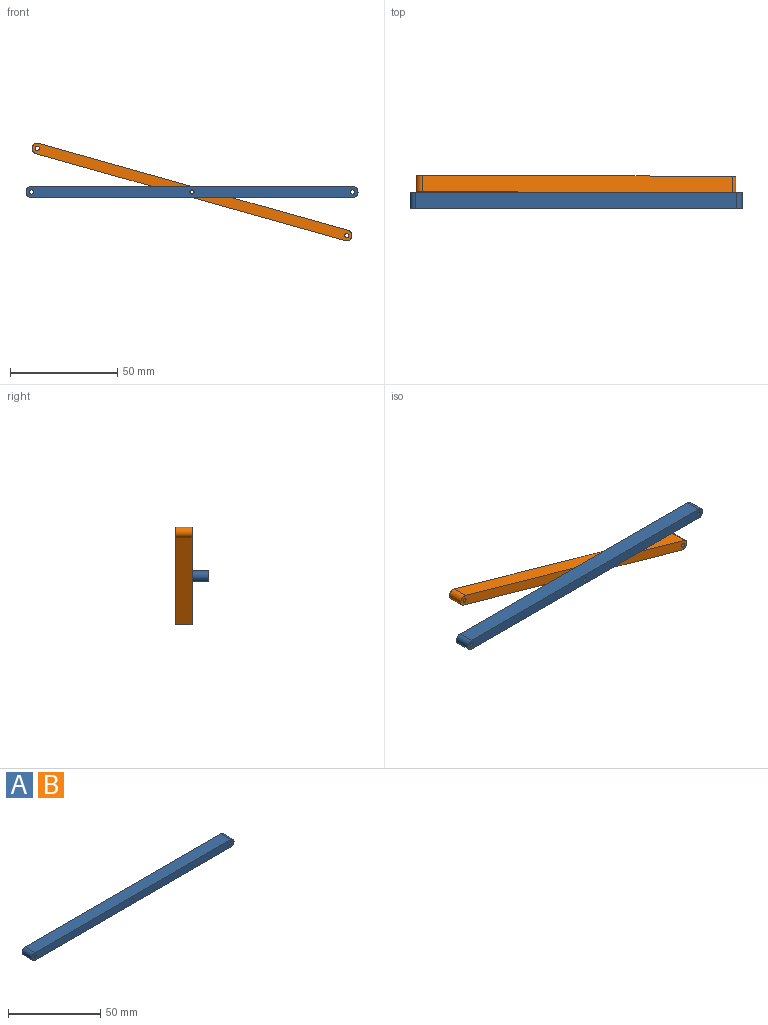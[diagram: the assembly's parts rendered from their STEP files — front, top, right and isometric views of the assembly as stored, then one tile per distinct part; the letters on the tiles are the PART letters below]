
ASSEMBLY  parts=2 mates=1
PART A: 9 faces, bbox 155x7.5x5 mm
  f0: plane 150x7.5mm, normal (0,0,1), area 1125mm2, adj f1,f6,f7,f8
  f1: cylinder r=2.5mm len=7.5mm, axis (0,1,0), area 58.9mm2, adj f0,f2,f7,f8
  f2: plane 150x7.5mm, normal (0,0,-1), area 1125mm2, adj f1,f6,f7,f8
  f3: cylinder r=1mm len=7.5mm, axis (0,1,0), area 47.1mm2, adj f7,f8
  f4: cylinder r=1mm len=7.5mm, axis (0,1,0), area 47.1mm2, adj f7,f8
  f5: cylinder r=1mm len=7.5mm, axis (0,1,0), area 47.1mm2, adj f7,f8
  f6: cylinder r=2.5mm len=7.5mm, axis (0,1,0), area 58.9mm2, adj f0,f2,f7,f8
  f7: plane 155x5mm, normal (0,-1,0), area 760.2mm2, adj f0,f1,f2,f3,f4,f5,f6
  f8: plane 155x5mm, normal (0,1,0), area 760.2mm2, adj f0,f1,f2,f3,f4,f5,f6
PART B: same geometry as A
PLACE A t=(-54.31,28.72,-8.01)mm
PLACE B rot(axis=(0,-1,0),164.3deg) t=(144.93,36.22,-13.53)mm
MATE revolute A.f5 <-> B.f5  axis (0,1,0) through (45.69,23.72,2.99)mm
